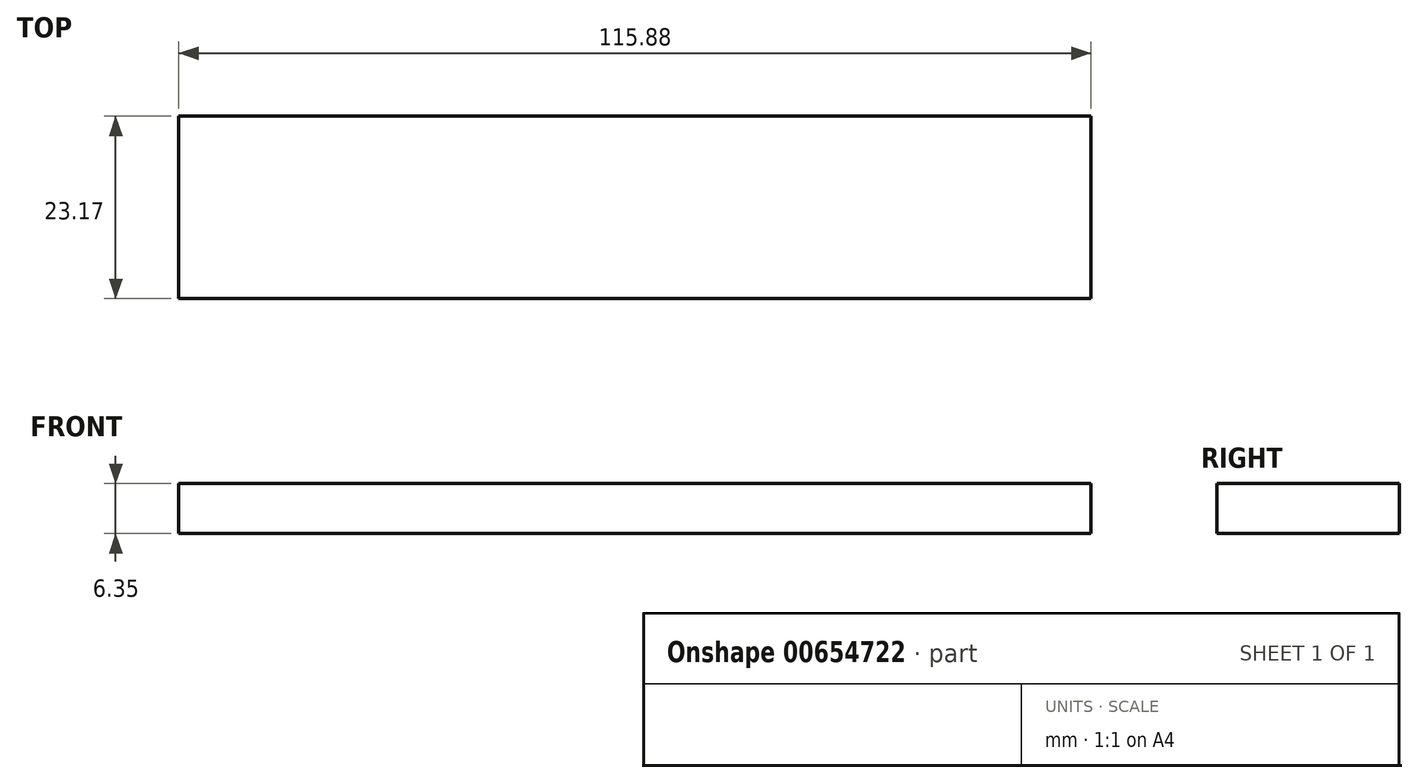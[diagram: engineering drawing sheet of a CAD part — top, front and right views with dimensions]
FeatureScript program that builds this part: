
annotation { "Feature Type Name" : "Feature", "Feature Type Description" : "" }
export const myFeature = defineFeature(function(context is Context, id is Id, definition is map)
    precondition{}
    {
        {
            var Q0;
            Q0=qCreatedBy(makeId("Top.planeOp"),FACE);
            var sketch = newSketch(context, id + "F0", { "sketchPlane" : qUnion([Q0])});
            skLineSegment(sketch, "E0", {"start": v(-56.39, 8.88) * mm, "end": v(59.49, 8.88) * mm});
            skLineSegment(sketch, "E1", {"start": v(-56.39, 32.05) * mm, "end": v(59.49, 32.05) * mm});
            skLineSegment(sketch, "E2", {"start": v(-56.39, 32.05) * mm, "end": v(-56.39, 8.88) * mm});
            skLineSegment(sketch, "E3", {"start": v(59.49, 32.05) * mm, "end": v(59.49, 8.88) * mm});
            skSolve(sketch);
        }
        {
            var Q0;
            Q0=makeQuery(id+"F0.imprint","IMPRINT",FACE,{"disambiguationData":[TD([[makeQuery(id+"F0.imprint","IMPRINT",EDGE,{"derivedFrom":sQuery(id+"F0.wireOp",EDGE,"E0")}),1.0]])]});
            extrude(context, id + "F1", {"entities" : qUnion([Q0]), "depth" : 6.35 * mm, "offsetDistance" : 25.4 * mm});
        }
    });
